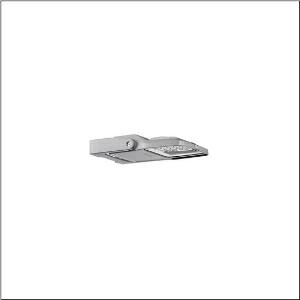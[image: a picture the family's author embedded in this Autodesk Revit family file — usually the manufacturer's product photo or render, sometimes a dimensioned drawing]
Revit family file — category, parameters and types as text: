
# Revit family: floodlight_fl_21_iq_micro___pl33t_5xa7761a4f2a_c8ff
name_source: partatom
category: Lighting Fixtures
units: mm (PartAtom-declared; Revit-internal decimal feet)

## family parameters
Cut with Voids When Loaded = No
Host = Face
Light Source = No
Part Type = Normal
Room Calculation Point = No
Round Connector Dimension = Use Diameter
Shared = No

## types (1)
- --- (1 x LED, 3050 lm, 23.1 W, 4000K)
    Apparent Load = 23 VA
    CIE Flux Codes = 26 75 99 100 100
    Color Rendering = 70
    Color Temperature = 4000K
    Default Elevation = 1800 mm
    Description = Floodlight FL 21 iQ micro, floodlight, primary light control with lens, of PMMA, primary optical cover: protective disc, of toughened safety glass, transparent, light distribution: PL33T, light emission: direct distribution, installation type: surface-mounted, LED, High Power LED, rated luminous flux: 3.050lm, luminous efficacy: 132lm/W, light colour: 740, colour temperature: 4000K, control: optimised constant luminous flux control (CLO 2.0), Desk-Remote (wireless, voltage-free reading and setting of iQ features in the workshop via application-optimized NFC function/RFID function), Light-Fading, Smart-Wire, Night-Set, Lumen-Switch, Temp-Guard, Auto-Match, with terminal, 6-pole, mains connection: 220..240V, AC, 50/60Hz, start of lifetime: 23W, end of service life: 24W, reduction: 11W, luminaire housing, of diecast aluminium, powder-coated, Siteco® metallic grey (DB 702S), corrosivity category C5 mid according to DIN EN ISO 12944, sealing non-destructively replaceable, design bracket, of diecast aluminium, powder-coated, Siteco® metallic grey (DB 702S), protection rating (complete): IP66, insulation class (complete): insulation class II (safety insulation), certification: CE, ENEC, VDE, protection symbol: D, impact resistance: IK07, permissible operating ambient temperature: -40..+40°C, permissible operating ambient temperature for outdoor applications: -40..+50°C, standard: DIN EN 12944, LABS conformity tested according to VDMA 24364:2018-05, packaging unit: 1 piece

Light Distribution: PL33T
    Height = 65 mm
    Lamp = 1 x LED
    Lamp Light Flux = 3050 lm
    Lamp Power = 23.1 W
    Lamp count = 1
    Length = 312 mm
    Luminous efficacy = 132 lm/W
    Manufacturer = Siteco
    ModVariant = No
    Model = 5XA7761A4F2A
    Mounting Place = Wall
    Mounting Type = Surface mounted
    Number of Poles = 1
    OnlyDefault = Yes
    Power Factor = 1
    Product Name = Floodlight FL 21 iQ micro | PL33T
    Product group = floodlight | wall mounted
    ProductGroupID = 2001
    Protection Class = Protection class II
    Protection Degree = IP 66
    RLX_Detail_Level = 1
    RLX_Emergency_Light_Flux = 0 lm
    RLX_Emergency_Type = 0
    RLX_Emergency_Type_DB = No
    RlxData = <blob elided: 97257 chars, md5=79a8f1a5>
    Socket = socket
    Standby Power = 0 W
    System Light Flux = 3050 lm
    System Power = 23 W
    Type Comments = factory setting: luminous flux: 100 % | dim-lin: 254 | 455 mA
    Type Image = l_1006878.jpg
    URL = http://relux.com
    VarID = @adj_118487
    Voltage = 0 V
    Weight = 0.00 kg
    Width = 230 mm

## geometry (parser evidence)
native form markers: Blend x4, Sweep x12
no freeform markers — native parametric forms only
